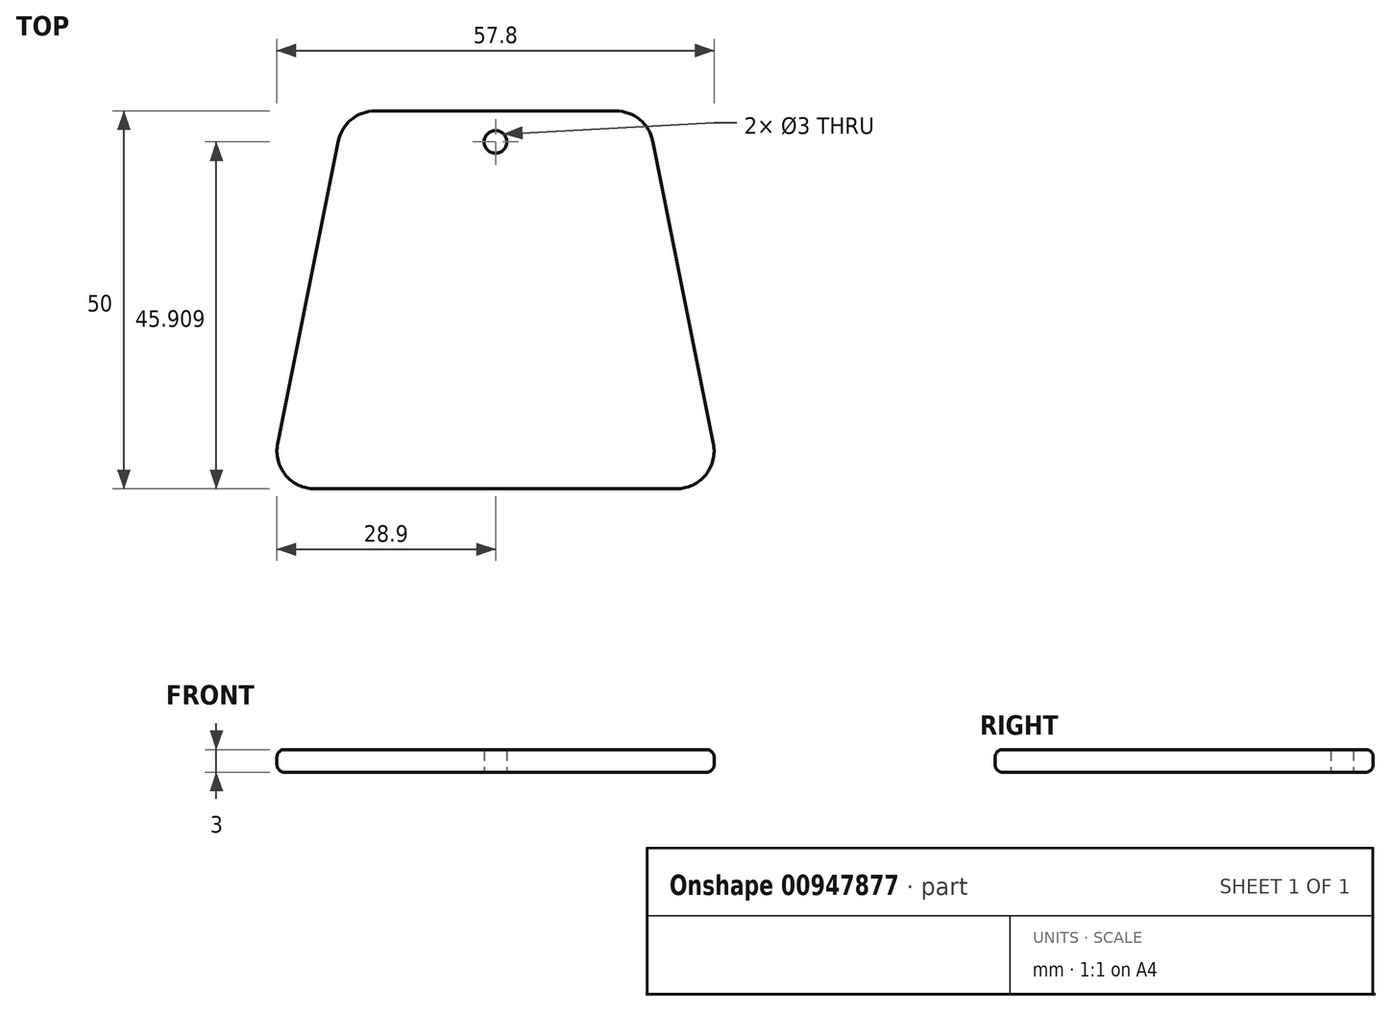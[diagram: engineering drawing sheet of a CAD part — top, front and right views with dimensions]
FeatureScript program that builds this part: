
annotation { "Feature Type Name" : "Feature", "Feature Type Description" : "" }
export const myFeature = defineFeature(function(context is Context, id is Id, definition is map)
    precondition{}
    {
        {
            var Q0;
            Q0=qCreatedBy(makeId("Top.planeOp"),FACE);
            var sketch = newSketch(context, id + "F0", { "sketchPlane" : qUnion([Q0])});
            skLineSegment(sketch, "E0", {"start": v(0, 0) * mm, "end": v(30, 0) * mm});
            skLineSegment(sketch, "E1", {"start": v(0, 50) * mm, "end": v(20, 50) * mm});
            skLineSegment(sketch, "E2", {"start": v(20, 50) * mm, "end": v(30, 0) * mm});
            skLineSegment(sketch, "E3.MirrorCS", {"start": v(0, 50) * mm, "end": v(-20, 50) * mm});
            skLineSegment(sketch, "E4.MirrorCS", {"start": v(-20, 50) * mm, "end": v(-30, 0) * mm});
            skLineSegment(sketch, "E5.MirrorCS", {"start": v(0, 0) * mm, "end": v(-30, 0) * mm});
            skCircle(sketch, "E6", {"center": v(0, 45.9) * mm, "radius": 1.5 * mm});
            skSolve(sketch);
        }
        {
            var Q0;
            Q0=makeQuery(id+"F0.imprint","IMPRINT",FACE,{"disambiguationData":[TD([[makeQuery(id+"F0.imprint","IMPRINT",EDGE,{"derivedFrom":sQuery(id+"F0.wireOp",EDGE,"E0")}),1.0]])]});
            extrude(context, id + "F1", {"entities" : qUnion([Q0]), "depth" : 3 * mm, "offsetDistance" : 25 * mm});
        }
        {
            var Q0;
            Q0=makeQuery(id+"F1.opExtrude","SWEPT_EDGE",EDGE,{"disambiguationData":[OSD([sQuery(id+"F0.wireOp",EDGE,"E3.MirrorCS"),sQuery(id+"F0.wireOp",EDGE,"E4.MirrorCS")])]});
            var Q1;
            Q1=makeQuery(id+"F1.opExtrude","SWEPT_EDGE",EDGE,{"disambiguationData":[OSD([sQuery(id+"F0.wireOp",EDGE,"E1"),sQuery(id+"F0.wireOp",EDGE,"E2")])]});
            var Q2;
            Q2=makeQuery(id+"F1.opExtrude","SWEPT_EDGE",EDGE,{"disambiguationData":[OSD([sQuery(id+"F0.wireOp",EDGE,"E0"),sQuery(id+"F0.wireOp",EDGE,"E2")])]});
            var Q3;
            Q3=makeQuery(id+"F1.opExtrude","SWEPT_EDGE",EDGE,{"disambiguationData":[OSD([sQuery(id+"F0.wireOp",EDGE,"E4.MirrorCS"),sQuery(id+"F0.wireOp",EDGE,"E5.MirrorCS")])]});
            fillet(context, id + "F2", {"entities" : qUnion([Q0, Q1, Q2, Q3]), "radius" : 5 * mm, "tangentPropagation" : true, "allowEdgeOverflow" : false});
        }
        {
            var Q0;
            Q0=makeQuery(id+"F1.opExtrude","CAP_EDGE",EDGE,{"disambiguationData":[OSD([sQuery(id+"F0.wireOp",EDGE,"E2")])],"isStart":false});
            var Q1;
            Q1=makeQuery(id+"F1.opExtrude","CAP_EDGE",EDGE,{"disambiguationData":[OSD([sQuery(id+"F0.wireOp",EDGE,"E2")])],"isStart":true});
            fillet(context, id + "F3", {"entities" : qUnion([Q0, Q1]), "radius" : 1 * mm, "tangentPropagation" : true, "allowEdgeOverflow" : false});
        }
    });
